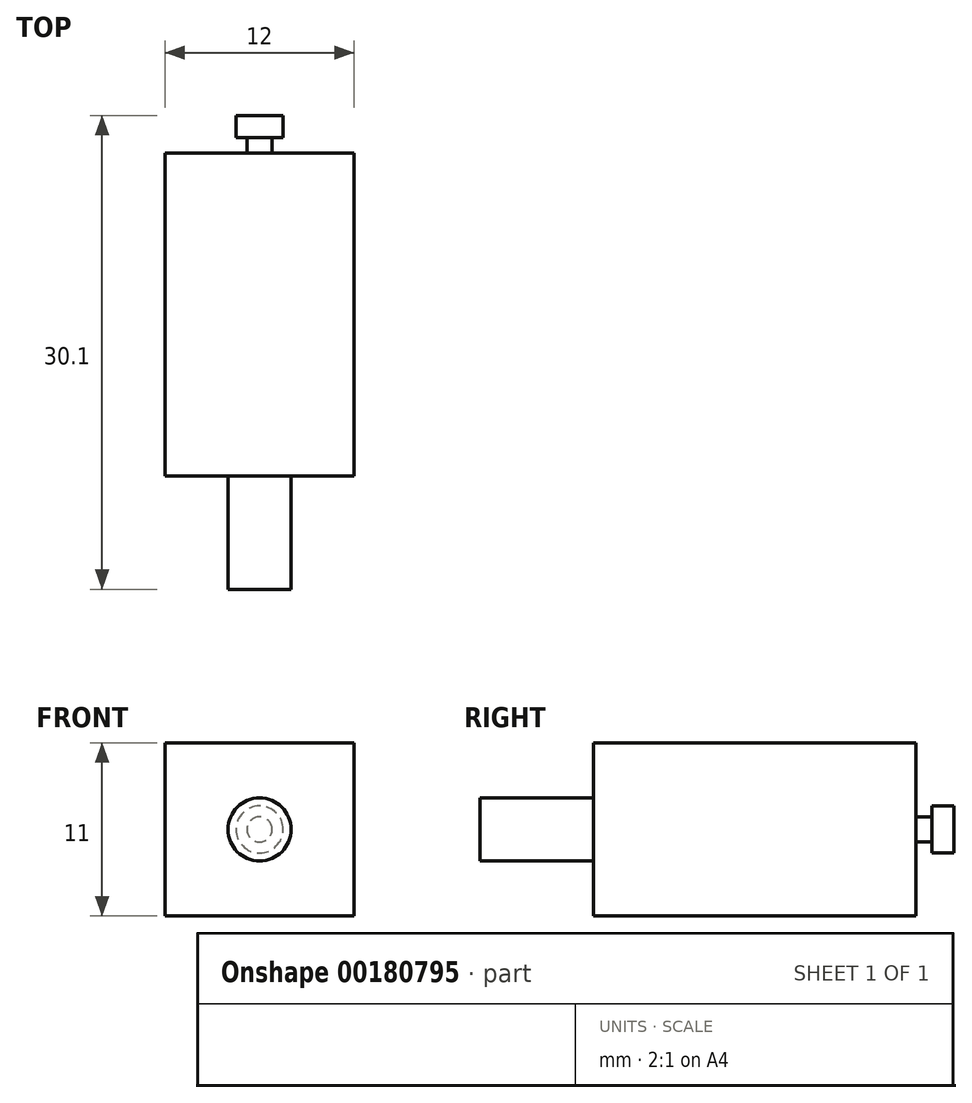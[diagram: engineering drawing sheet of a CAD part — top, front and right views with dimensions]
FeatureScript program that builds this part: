
annotation { "Feature Type Name" : "Feature", "Feature Type Description" : "" }
export const myFeature = defineFeature(function(context is Context, id is Id, definition is map)
    precondition{}
    {
        {
            var Q0;
            Q0=qCreatedBy(makeId("Front.planeOp"),FACE);
            var sketch = newSketch(context, id + "F0", { "sketchPlane" : qUnion([Q0])});
            skLineSegment(sketch, "E0.bottom", {"start": v(6, 5.5) * mm, "end": v(-6, 5.5) * mm});
            skLineSegment(sketch, "E0.top", {"start": v(6, -5.5) * mm, "end": v(-6, -5.5) * mm});
            skLineSegment(sketch, "E0.left", {"start": v(6, 5.5) * mm, "end": v(6, -5.5) * mm});
            skLineSegment(sketch, "E0.right", {"start": v(-6, 5.5) * mm, "end": v(-6, -5.5) * mm});
            skPoint(sketch, "E0.middle", {"position": v(0, 0) * mm});
            skSolve(sketch);
        }
        {
            var Q0;
            Q0 = qSketchRegion(id + "F0", true);
            extrude(context, id + "F1", {"entities" : qUnion([Q0]), "depth" : 20.5 * mm});
        }
        {
            var Q0;
            Q0=makeQuery(id+"F1.opExtrude","CAP_FACE",FACE,{"disambiguationData":[OSD([sQuery(id+"F0.wireOp",EDGE,"E0.bottom"),sQuery(id+"F0.wireOp",EDGE,"E0.top"),sQuery(id+"F0.wireOp",EDGE,"E0.left"),sQuery(id+"F0.wireOp",EDGE,"E0.right")])],"isStart":false});
            var sketch = newSketch(context, id + "F2", { "sketchPlane" : qUnion([Q0])});
            skCircle(sketch, "E1", {"center": v(0, 0) * mm, "radius": 2 * mm});
            skSolve(sketch);
        }
        {
            var Q0;
            Q0 = qSketchRegion(id + "F2", true);
            extrude(context, id + "F3", {"entities" : qUnion([Q0]), "operationType" : NewBodyOperationType.ADD, "depth" : 7.2 * mm});
        }
        {
            var Q0;
            Q0=makeQuery(id+"F1.opExtrude","CAP_FACE",FACE,{"disambiguationData":[OSD([sQuery(id+"F0.wireOp",EDGE,"E0.bottom"),sQuery(id+"F0.wireOp",EDGE,"E0.top"),sQuery(id+"F0.wireOp",EDGE,"E0.left"),sQuery(id+"F0.wireOp",EDGE,"E0.right")])],"isStart":true});
            var sketch = newSketch(context, id + "F4", { "sketchPlane" : qUnion([Q0])});
            skCircle(sketch, "E2", {"center": v(0, 0) * mm, "radius": 0.8 * mm});
            skSolve(sketch);
        }
        {
            var Q0;
            Q0=makeQuery(id+"F4.imprint","IMPRINT",FACE,{"disambiguationData":[TD([[makeQuery(id+"F4.imprint","IMPRINT",EDGE,{"derivedFrom":sQuery(id+"F4.wireOp",EDGE,"E2")}),1.0]])]});
            extrude(context, id + "F5", {"entities" : qUnion([Q0]), "operationType" : NewBodyOperationType.ADD, "depth" : 1 * mm});
        }
        {
            var Q0;
            Q0=makeQuery(id+"F5.opExtrude","CAP_FACE",FACE,{"disambiguationData":[OSD([sQuery(id+"F4.wireOp",EDGE,"E2")])],"isStart":false});
            var sketch = newSketch(context, id + "F6", { "sketchPlane" : qUnion([Q0])});
            skCircle(sketch, "E3", {"center": v(0, 0) * mm, "radius": 1.5 * mm});
            skSolve(sketch);
        }
        {
            var Q0;
            Q0=makeQuery(id+"F6.imprint","IMPRINT",FACE,{"disambiguationData":[TD([[makeQuery(id+"F6.imprint","IMPRINT",EDGE,{"derivedFrom":makeQuery(id+"F5.opExtrude","CAP_EDGE",EDGE,{"disambiguationData":[OSD([sQuery(id+"F4.wireOp",EDGE,"E2")])],"isStart":false})}),1.0]])]});
            var Q1;
            Q1=makeQuery(id+"F6.imprint","IMPRINT",FACE,{"disambiguationData":[TD([[makeQuery(id+"F6.imprint","IMPRINT",EDGE,{"derivedFrom":sQuery(id+"F6.wireOp",EDGE,"E3")}),1.0]])]});
            extrude(context, id + "F7", {"entities" : qUnion([Q0, Q1]), "operationType" : NewBodyOperationType.ADD, "depth" : 1.4 * mm});
        }
    });
